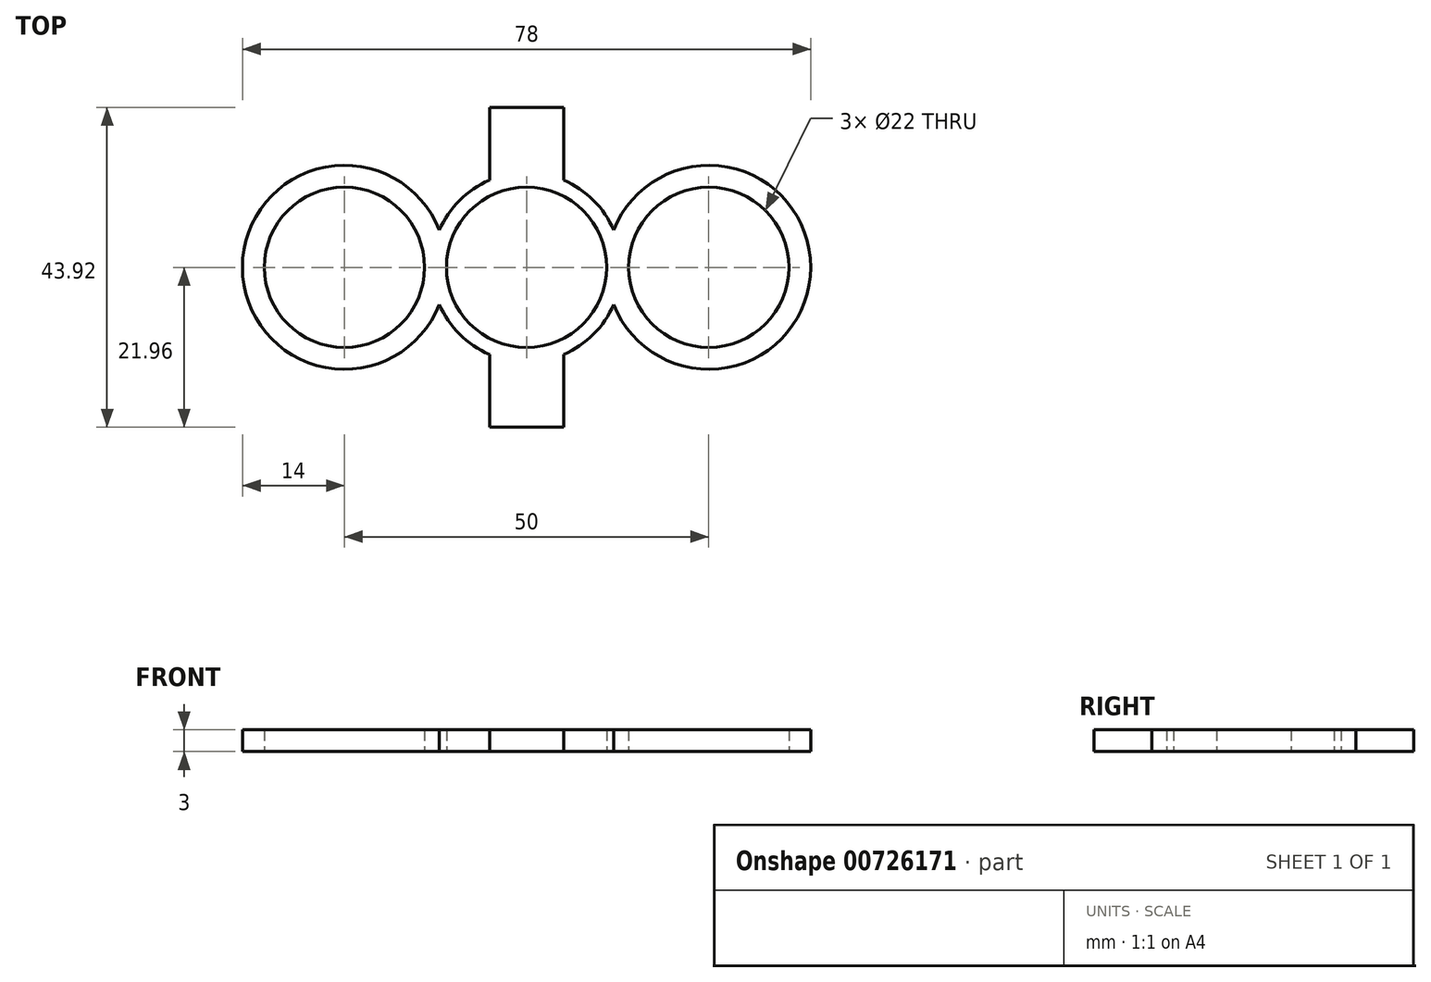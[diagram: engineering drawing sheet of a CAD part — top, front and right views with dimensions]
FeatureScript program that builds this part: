
annotation { "Feature Type Name" : "Feature", "Feature Type Description" : "" }
export const myFeature = defineFeature(function(context is Context, id is Id, definition is map)
    precondition{}
    {
        {
            var Q0;
            Q0=qCreatedBy(makeId("Top.planeOp"),FACE);
            var sketch = newSketch(context, id + "F0", { "sketchPlane" : qUnion([Q0])});
            skCircle(sketch, "E0", {"center": v(0, 0) * mm, "radius": 11 * mm});
            skArc(sketch, "E1", {"start": v(-5.1, 11.96) * mm, "mid": v(-9.2, 9.2) * mm, "end": v(-11.96, 5.1) * mm});
            skLineSegment(sketch, "E2", {"start": v(0, -13) * mm, "end": v(0, -14) * mm});
            skPoint(sketch, "E2.endSnap0", {"position": v(0, -13) * mm});
            skArc(sketch, "E3.trimOffspring", {"start": v(5.1, -11.96) * mm, "mid": v(9.2, -9.2) * mm, "end": v(11.96, -5.1) * mm});
            skPoint(sketch, "E4.endSnap0", {"position": v(-13, 0) * mm});
            skCircle(sketch, "E5", {"center": v(-25, 0) * mm, "radius": 11 * mm});
            skArc(sketch, "E6", {"start": v(-11.96, 5.1) * mm, "mid": v(-39, 0) * mm, "end": v(-11.96, -5.1) * mm});
            skArc(sketch, "E7.trimOffspring", {"start": v(-11.96, -5.1) * mm, "mid": v(-9.2, -9.2) * mm, "end": v(-5.1, -11.96) * mm});
            skCircle(sketch, "E8", {"center": v(25, 0) * mm, "radius": 11 * mm});
            skArc(sketch, "E9", {"start": v(11.96, -5.1) * mm, "mid": v(39, 0) * mm, "end": v(11.96, 5.1) * mm});
            skArc(sketch, "E10.trimOffspring", {"start": v(11.96, 5.1) * mm, "mid": v(9.2, 9.2) * mm, "end": v(5.1, 11.96) * mm});
            skLineSegment(sketch, "E11", {"start": v(-5.1, 11.96) * mm, "end": v(5.1, 11.96) * mm});
            skLineSegment(sketch, "E12", {"start": v(5.1, -11.96) * mm, "end": v(-5.1, -11.96) * mm});
            skLineSegment(sketch, "E13", {"start": v(-5.1, 11.96) * mm, "end": v(-5.1, 21.96) * mm});
            skLineSegment(sketch, "E14", {"start": v(5.1, 11.96) * mm, "end": v(5.1, 21.96) * mm});
            skLineSegment(sketch, "E15", {"start": v(5.1, 21.96) * mm, "end": v(-5.1, 21.96) * mm});
            skLineSegment(sketch, "E16", {"start": v(-5.1, -11.96) * mm, "end": v(-5.1, -21.96) * mm});
            skLineSegment(sketch, "E17", {"start": v(5.1, -11.96) * mm, "end": v(5.1, -21.96) * mm});
            skLineSegment(sketch, "E18", {"start": v(5.1, -21.96) * mm, "end": v(-5.1, -21.96) * mm});
            skSolve(sketch);
        }
        {
            var Q0;
            Q0 = qSketchRegion(id + "F0", true);
            extrude(context, id + "F1", {"entities" : qUnion([Q0]), "depth" : 3 * mm, "offsetDistance" : 25 * mm});
        }
    });
